# Revit family: TESK_Насос вертикальный с овальными фланцами_SVMT-10
name_source: partatom
category: Оборудование
units: mm (PartAtom-declared; Revit-internal decimal feet)

## family parameters
Всегда вертикально = Да
Классификация = Насос
На основе рабочей плоскости = Нет
Общий = Нет
При загрузке вырезать с полостями = Нет
Размер круглого соединителя = Использовать диаметр
Тип детали = Вставляется
Точка расчета площади = Нет

## types (15) — shared parameters
ADSK_Версия Revit = 2019
ADSK_Версия семейства = 1.0
ADSK_Диаметр условный = 40 мм
ADSK_Единица измерения = шт.
ADSK_Завод-изготовитель = TESK
ADSK_Классификация нагрузок = Прочее
ADSK_Количество = 1
ADSK_Количество фаз = 3
ADSK_Количество фаз числовое = 3
ADSK_Коэффициент мощности = 1
ADSK_Наименование краткое = Вертикальный многоступенчатый центробежный насос
ADSK_Напряжение = 400 В
URL = www.teskpump.ru
Длина_ВспомЛиния = 30 мм
Материал_1 = TESK_Черный_Условный
Материал_2 = TESK_Нержавеющая сталь
Материал_КорпусДвигателя = TESK_Черный_Ребра_Условный
Материал_КорпусУлитка = TESK_Черный_Условный
Таблица_Поиска = TESK_SVMT-10 ОФ
УГО_Длина = 244 мм
Фланец_Толщина = 22 мм

## per-type parameters (varying)
| type | ADSK_Код изделия | ADSK_Масса | ADSK_Масса_Текст | ADSK_Наименование | ADSK_Номинальная мощность | ADSK_Полная мощность | Высота_Корпуса | Высота_Перехода | Двигатель_Высота | Двигатель_ОтступКоробки | Двигатель_Ширина | Напор максимальный |
| SVMT 10-2 0.75kW 3x380V 50Hz IE3 | 7710-20003380NF | 32 | 32 | Вертикальный многоступенчатый центробежный насос SVMT, DN40, Hmax=18.5м (3x380V 50Hz IE3) | 1 кВт | 1 кВ·А | 347 мм | 130 мм | 280 мм | 142 мм | 170 мм | 18.5 |
| SVMT 10-3 1.1kW 3x380V 50Hz IE3 | 7710-30003380NF | 34 | 34 | Вертикальный многоступенчатый центробежный насос SVMT, DN40, Hmax=30м (3x380V 50Hz IE3) | 1 кВт | 1 кВ·А | 377 мм | 130 мм | 280 мм | 142 мм | 170 мм | 30 |
| SVMT 10-4 1.5kW 3x380V 50Hz IE3 | 7710-40003380NF | 40 | 40 | Вертикальный многоступенчатый центробежный насос SVMT, DN40, Hmax=40.5м (3x380V 50Hz IE3) | 2 кВт | 2 кВ·А | 417 мм | 150 мм | 333 мм | 155 мм | 190 мм | 40.5 |
| SVMT 10-5 2.2kW 3x380V 50Hz IE3 | 7710-50003380NF | 44 | 44 | Вертикальный многоступенчатый центробежный насос SVMT, DN40, Hmax=50м (3x380V 50Hz IE3) | 2 кВт | 2 кВ·А | 447 мм | 150 мм | 333 мм | 155 мм | 190 мм | 50 |
| SVMT 10-6 2.2kW 3x380V 50Hz IE3 | 7710-60003380NF | 45 | 45 | Вертикальный многоступенчатый центробежный насос SVMT, DN40, Hmax=60м (3x380V 50Hz IE3) | 2 кВт | 2 кВ·А | 477 мм | 150 мм | 333 мм | 155 мм | 190 мм | 60 |
| SVMT 10-7 3kW 3x380V 50Hz IE3 | 7710-70003380NF | 52 | 52 | Вертикальный многоступенчатый центробежный насос SVMT, DN40, Hmax=70.5м (3x380V 50Hz IE3) | 3 кВт | 3 кВ·А | 517 мм | 170 мм | 348 мм | 165 мм | 197 мм | 70.5 |
| SVMT 10-8 3kW 3x380V 50Hz IE3 | 7710-80003380NF | 53 | 53 | Вертикальный многоступенчатый центробежный насос SVMT, DN40, Hmax=81м (3x380V 50Hz IE3) | 3 кВт | 3 кВ·А | 547 мм | 170 мм | 348 мм | 165 мм | 197 мм | 81 |
| SVMT 10-9 3kW 3x380V 50Hz IE3 | 7710-90003380NF | 54 | 54 | Вертикальный многоступенчатый центробежный насос SVMT, DN40, Hmax=91м (3x380V 50Hz IE3) | 3 кВт | 3 кВ·А | 577 мм | 170 мм | 348 мм | 165 мм | 197 мм | 91 |
| SVMT 10-10 4kW 3x380V 50Hz IE3 | 7710-100003380NF | 64 | 64 | Вертикальный многоступенчатый центробежный насос SVMT, DN40, Hmax=101.5м (3x380V 50Hz IE3) | 4 кВт | 4 кВ·А | 607 мм | 190 мм | 382 мм | 185 мм | 230 мм | 101.5 |
| SVMT 10-12 4kW 3x380V 50Hz IE3 | 7710-120003380NF | 66 | 66 | Вертикальный многоступенчатый центробежный насос SVMT, DN40, Hmax=120.5м (3x380V 50Hz IE3) | 4 кВт | 4 кВ·А | 667 мм | 190 мм | 382 мм | 185 мм | 230 мм | 120.5 |
| SVMT 10-14 5.5kW 3x380V 50Hz IE3 | 7710-140003380NF | 81 | 81 | Вертикальный многоступенчатый центробежный насос SVMT, DN40, Hmax=142м (3x380V 50Hz IE3) | 6 кВт | 6 кВ·А | 747 мм | 210 мм | 435 мм | 210 мм | 260 мм | 142 |
| SVMT 10-16 5.5kW 3x380V 50Hz IE3 | 7710-160003380NF | 82 | 82 | Вертикальный многоступенчатый центробежный насос SVMT, DN40, Hmax=162м (3x380V 50Hz IE3) | 6 кВт | 6 кВ·А | 807 мм | 210 мм | 435 мм | 210 мм | 260 мм | 162 |
| SVMT 10-18 7.5kW 3x380V 50Hz IE3 | 7710-180003380NF | 93 | 93 | Вертикальный многоступенчатый центробежный насос SVMT, DN40, Hmax=183м (3x380V 50Hz IE3) | 8 кВт | 8 кВ·А | 867 мм | 210 мм | 435 мм | 210 мм | 260 мм | 183 |
| SVMT 10-20 7.5kW 3x380V 50Hz IE3 | 7710-200003380NF | 94 | 94 | Вертикальный многоступенчатый центробежный насос SVMT, DN40, Hmax=203м (3x380V 50Hz IE3) | 8 кВт | 8 кВ·А | 927 мм | 210 мм | 435 мм | 210 мм | 260 мм | 203 |
| SVMT 10-22 7.5kW 3x380V 50Hz IE3 | 7710-220003380NF | 95 | 95 | Вертикальный многоступенчатый центробежный насос SVMT, DN40, Hmax=222м (3x380V 50Hz IE3) | 8 кВт | 8 кВ·А | 987 мм | 210 мм | 435 мм | 210 мм | 260 мм | 222 |

note: column(s) folded — value = type name in every type: ADSK_Марка
